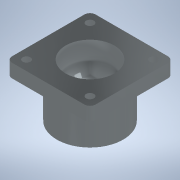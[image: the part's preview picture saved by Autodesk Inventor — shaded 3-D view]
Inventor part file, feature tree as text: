
AUTODESK INVENTOR PART (.ipt)
format: ipt  version: 2022.1 (Build 261234000, 234)  size: 140,800 bytes
history: native  units: mm (DEFAULTED — no unit token found)
features: other x8, sketch x4, extrude x3, fillet x1, plane x1, revolve x1, projected_geometry x1
bodies: Body1 (feature_tree)
feature tree (19):
  other  "Sólido1"
  other  "Origen"
  extrude  "Extrusión1"  Depth=48.2mm TaperAngle=0.0deg
  extrude  "Extrusión2"  Depth=12.4mm TaperAngle=0.0deg
  extrude  "Extrusión3"  Depth=7.1mm
  fillet  "Empalme1"  [1 undecoded]
  plane  "Plano de trabajo1"
  revolve  "Revolución1"  [1 undecoded]
  other  "Plano YZ"
  other  "Plano XZ"
  other  "Plano XY"
  other  "Eje X"
  other  "Eje Y"
  other  "Eje Z"
  sketch  "Boceto1"  dims[d0=60.5mm d1=48.2mm d2=0.0mm]
  sketch  "Boceto2"  dims[d3=76.2mm d4=12.4mm d5=0.0mm]
  sketch  "Boceto3"  dims[d7=57.9mm d8=7.1mm d9=0.0mm d10=0.0mm]
  projected_geometry  "Contorno proyectado1"
  sketch  "Boceto4"  dims[d11=5.0mm d12=-35.8mm d13=50.8mm d14=360.0deg]
note: 2 required parameter values undecoded (feature->parameter linkage not recoverable at this tier; creation-order binding heuristic only, values carry confidence <= 0.55)